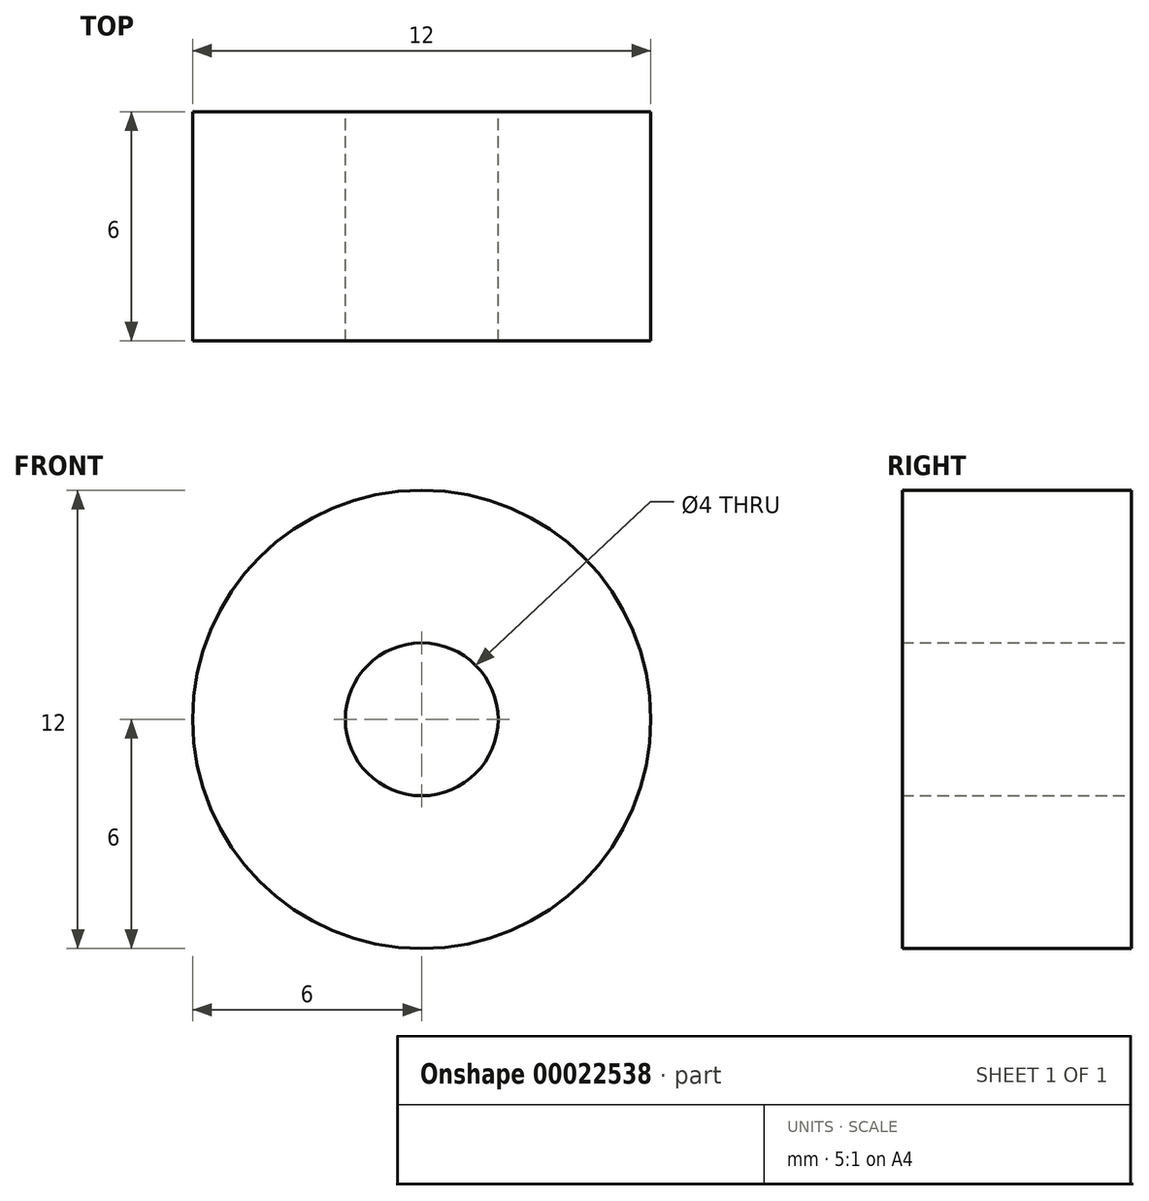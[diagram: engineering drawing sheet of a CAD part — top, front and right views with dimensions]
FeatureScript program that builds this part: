
annotation { "Feature Type Name" : "Feature", "Feature Type Description" : "" }
export const myFeature = defineFeature(function(context is Context, id is Id, definition is map)
    precondition{}
    {
        {
            var Q0;
            Q0=qCreatedBy(makeId("Front.planeOp"),FACE);
            var sketch = newSketch(context, id + "F0", { "sketchPlane" : qUnion([Q0])});
            skCircle(sketch, "E0", {"center": v(0, 0) * mm, "radius": 6 * mm});
            skCircle(sketch, "E1", {"center": v(0, 0) * mm, "radius": 2 * mm});
            skSolve(sketch);
        }
        {
            var Q0;
            Q0=makeQuery(id+"F0.imprint","IMPRINT",FACE,{"disambiguationData":[TD([[makeQuery(id+"F0.imprint","IMPRINT",EDGE,{"derivedFrom":sQuery(id+"F0.wireOp",EDGE,"E0")}),1.0]])]});
            extrude(context, id + "F1", {"entities" : qUnion([Q0]), "depth" : 6 * mm});
        }
    });
